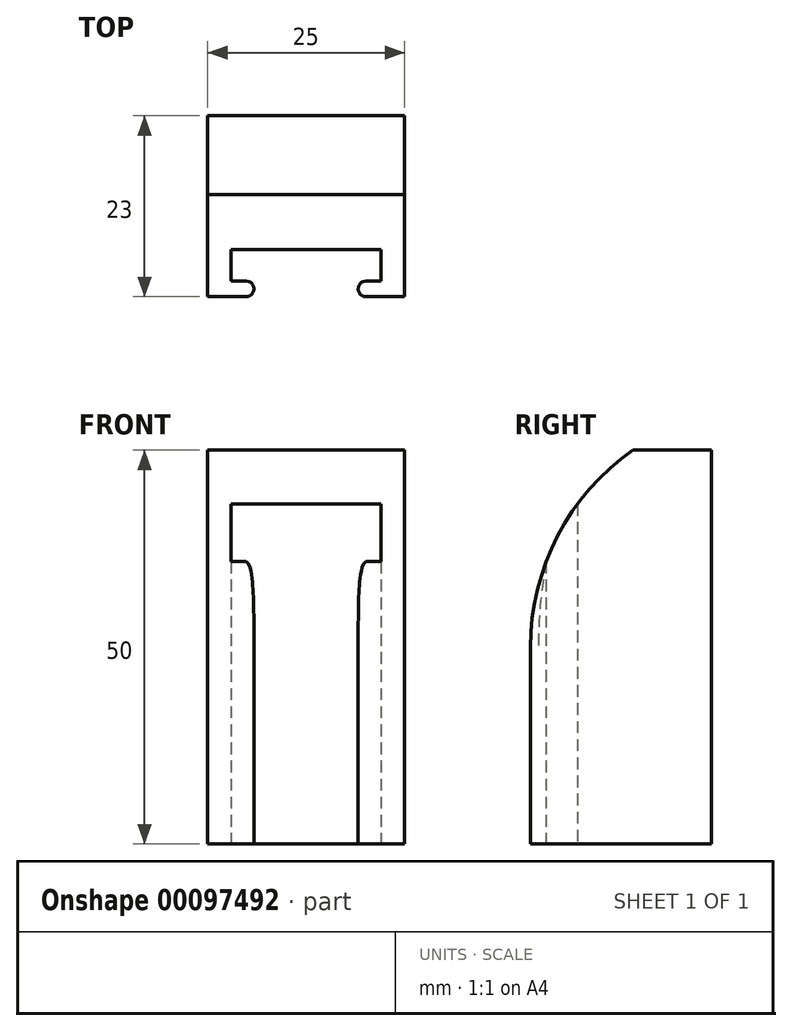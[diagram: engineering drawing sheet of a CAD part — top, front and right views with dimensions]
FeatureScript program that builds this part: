
annotation { "Feature Type Name" : "Feature", "Feature Type Description" : "" }
export const myFeature = defineFeature(function(context is Context, id is Id, definition is map)
    precondition{}
    {
        {
            var Q0;
            Q0=qCreatedBy(makeId("Top.planeOp"),FACE);
            var sketch = newSketch(context, id + "F0", { "sketchPlane" : qUnion([Q0])});
            skLineSegment(sketch, "E0", {"start": v(0, 0) * mm, "end": v(-9.5, 0) * mm});
            skLineSegment(sketch, "E1", {"start": v(0, 0) * mm, "end": v(0, -23.25) * mm, "construction": true});
            skLineSegment(sketch, "E2.MirrorCS", {"start": v(0, 0) * mm, "end": v(9.5, 0) * mm});
            skLineSegment(sketch, "E3", {"start": v(-9.5, 0) * mm, "end": v(-9.5, -4) * mm});
            skLineSegment(sketch, "E4", {"start": v(-9.5, -4) * mm, "end": v(-6.62, -4) * mm});
            skLineSegment(sketch, "E5", {"start": v(-6.62, -4) * mm, "end": v(-6.62, -6) * mm});
            skLineSegment(sketch, "E6", {"start": v(-6.62, -6) * mm, "end": v(-12.5, -6) * mm});
            skLineSegment(sketch, "E7.MirrorCS", {"start": v(9.5, 0) * mm, "end": v(9.5, -4) * mm});
            skLineSegment(sketch, "E8.MirrorCS", {"start": v(9.5, -4) * mm, "end": v(6.62, -4) * mm});
            skLineSegment(sketch, "E9.MirrorCS", {"start": v(6.63, -4) * mm, "end": v(6.63, -6) * mm});
            skLineSegment(sketch, "E10.MirrorCS", {"start": v(6.62, -6) * mm, "end": v(12.5, -6) * mm});
            skLineSegment(sketch, "E11", {"start": v(-12.5, -6) * mm, "end": v(-12.5, 7) * mm});
            skLineSegment(sketch, "E12", {"start": v(-12.5, 7) * mm, "end": v(0, 7) * mm});
            skLineSegment(sketch, "E13.MirrorCS", {"start": v(12.5, -6) * mm, "end": v(12.5, 7) * mm});
            skLineSegment(sketch, "E14.MirrorCS", {"start": v(12.5, 7) * mm, "end": v(0, 7) * mm});
            skSolve(sketch);
        }
        {
            var Q0;
            Q0=makeQuery(id+"F0.imprint","IMPRINT",FACE,{"disambiguationData":[TD([[makeQuery(id+"F0.imprint","IMPRINT",EDGE,{"derivedFrom":sQuery(id+"F0.wireOp",EDGE,"E0")}),-1.0]])]});
            extrude(context, id + "F1", {"entities" : qUnion([Q0]), "depth" : 50 * mm});
        }
        {
            var Q0;
            Q0=makeQuery(id+"F1.opExtrude","SWEPT_FACE",FACE,{"disambiguationData":[OSD([sQuery(id+"F0.wireOp",EDGE,"E13.MirrorCS")])]});
            var sketch = newSketch(context, id + "F2", { "sketchPlane" : qUnion([Q0])});
            skArc(sketch, "E15", {"start": v(7, 50) * mm, "mid": v(-2.56, 39.09) * mm, "end": v(-6, 25) * mm});
            skSolve(sketch);
        }
        {
            var Q0;
            {var subQ0=sQuery(id+"F2.wireOp",EDGE,"E15");Q0=makeQuery(id+"F2.imprint","IMPRINT",FACE,{"disambiguationData":[TD([[makeQuery(id+"F2.imprint","IMPRINT",EDGE,{"derivedFrom":subQ0}),-1.0]])]});}
            var Q1;
            Q1=makeQuery(id+"F1.opExtrude","SWEPT_FACE",FACE,{"disambiguationData":[OSD([sQuery(id+"F0.wireOp",EDGE,"E11")])]});
            extrude(context, id + "F3", {"entities" : qUnion([Q0]), "operationType" : NewBodyOperationType.REMOVE, "endBound" : BoundingType.UP_TO_SURFACE, "oppositeDirection" : true, "endBoundEntityFace" : qUnion([Q1]), "depth" : 25 * mm});
        }
        {
            var Q0;
            Q0=makeQuery(id+"F1.opExtrude","SWEPT_EDGE",EDGE,{"disambiguationData":[OSD([sQuery(id+"F0.wireOp",EDGE,"E5"),sQuery(id+"F0.wireOp",EDGE,"E6")])]});
            var Q1;
            Q1=makeQuery(id+"F1.opExtrude","SWEPT_EDGE",EDGE,{"disambiguationData":[OSD([sQuery(id+"F0.wireOp",EDGE,"E4"),sQuery(id+"F0.wireOp",EDGE,"E5")])]});
            var Q2;
            Q2=makeQuery(id+"F1.opExtrude","SWEPT_EDGE",EDGE,{"disambiguationData":[OSD([sQuery(id+"F0.wireOp",EDGE,"E9.MirrorCS"),sQuery(id+"F0.wireOp",EDGE,"E10.MirrorCS")])]});
            var Q3;
            Q3=makeQuery(id+"F1.opExtrude","SWEPT_EDGE",EDGE,{"disambiguationData":[OSD([sQuery(id+"F0.wireOp",EDGE,"E8.MirrorCS"),sQuery(id+"F0.wireOp",EDGE,"E9.MirrorCS")])]});
            var Q4;
            Q4=makeQuery(id+"F3.boolean.opBoolean","COPY",EDGE,{"derivedFrom":makeQuery(id+"F3.opExtrude","CAP_EDGE",EDGE,{"disambiguationData":[OSD([sQuery(id+"F2.wireOp",EDGE,"E15")])],"isStart":false})});
            var Q5;
            Q5=makeQuery(id+"F3.boolean.opBoolean","COPY",EDGE,{"derivedFrom":makeQuery(id+"F3.opExtrude","CAP_EDGE",EDGE,{"disambiguationData":[OSD([sQuery(id+"F2.wireOp",EDGE,"E15")])],"isStart":true})});
            fillet(context, id + "F4", {"entities" : qUnion([Q0, Q1, Q2, Q3, Q4, Q5]), "radius" : 1 * mm, "tangentPropagation" : true, "allowEdgeOverflow" : false});
        }
        {
            var Q0;
            Q0=makeQuery(id+"F1.opExtrude","SWEPT_FACE",FACE,{"disambiguationData":[OSD([sQuery(id+"F0.wireOp",EDGE,"E12"),sQuery(id+"F0.wireOp",EDGE,"E14.MirrorCS")])]});
            extrude(context, id + "F5", {"entities" : qUnion([Q0]), "operationType" : NewBodyOperationType.ADD, "depth" : 10 * mm});
        }
    });
